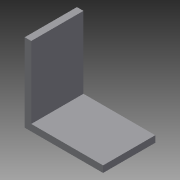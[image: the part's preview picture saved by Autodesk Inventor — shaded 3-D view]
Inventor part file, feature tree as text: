
AUTODESK INVENTOR PART (.ipt)
format: ipt  version: 2015 (Build 190159000, 159)  size: 82,944 bytes
history: native  units: in
note: dims shown in document units (in); Inventor stores cm internally (conversion verified against a paired STEP export)
features: extrude x2, sketch x2
ambient origin geometry x8: Origin, YZ Plane, XZ Plane, XY Plane, X Axis, Y Axis, Z Axis, Center Point
bodies: Solid1 (feature_tree)
feature tree (4):
  extrude  "Extrusion1"  Depth=0.125in
  extrude  "Extrusion2"  Depth=0.125in
  sketch  "Sketch1"  dims[d0=1.5in d1=0.125in]
  sketch  "Sketch2"  dims[d2=1.0in d3=0.0in d4=0.125in d5=1.5in d6=1.0in d7=0.0in]
